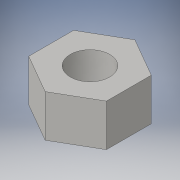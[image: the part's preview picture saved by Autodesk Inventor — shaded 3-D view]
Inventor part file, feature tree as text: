
AUTODESK INVENTOR PART (.ipt)
format: ipt  version: 2016 (Build 200138000, 138)  size: 93,696 bytes
history: native  units: in
note: dims shown in document units (in); Inventor stores cm internally (conversion verified against a paired STEP export)
features: extrude x1, sketch x1
ambient origin geometry x8: Origin, YZ Plane, XZ Plane, XY Plane, X Axis, Y Axis, Z Axis, Center Point
bodies: Solid1 (feature_tree)
feature tree (2):
  extrude  "Extrusion1"  Depth=0.375in
  sketch  "Sketch1"  dims[d0=0.19in d1=0.375in d2=0.203in d3=0.0in]
